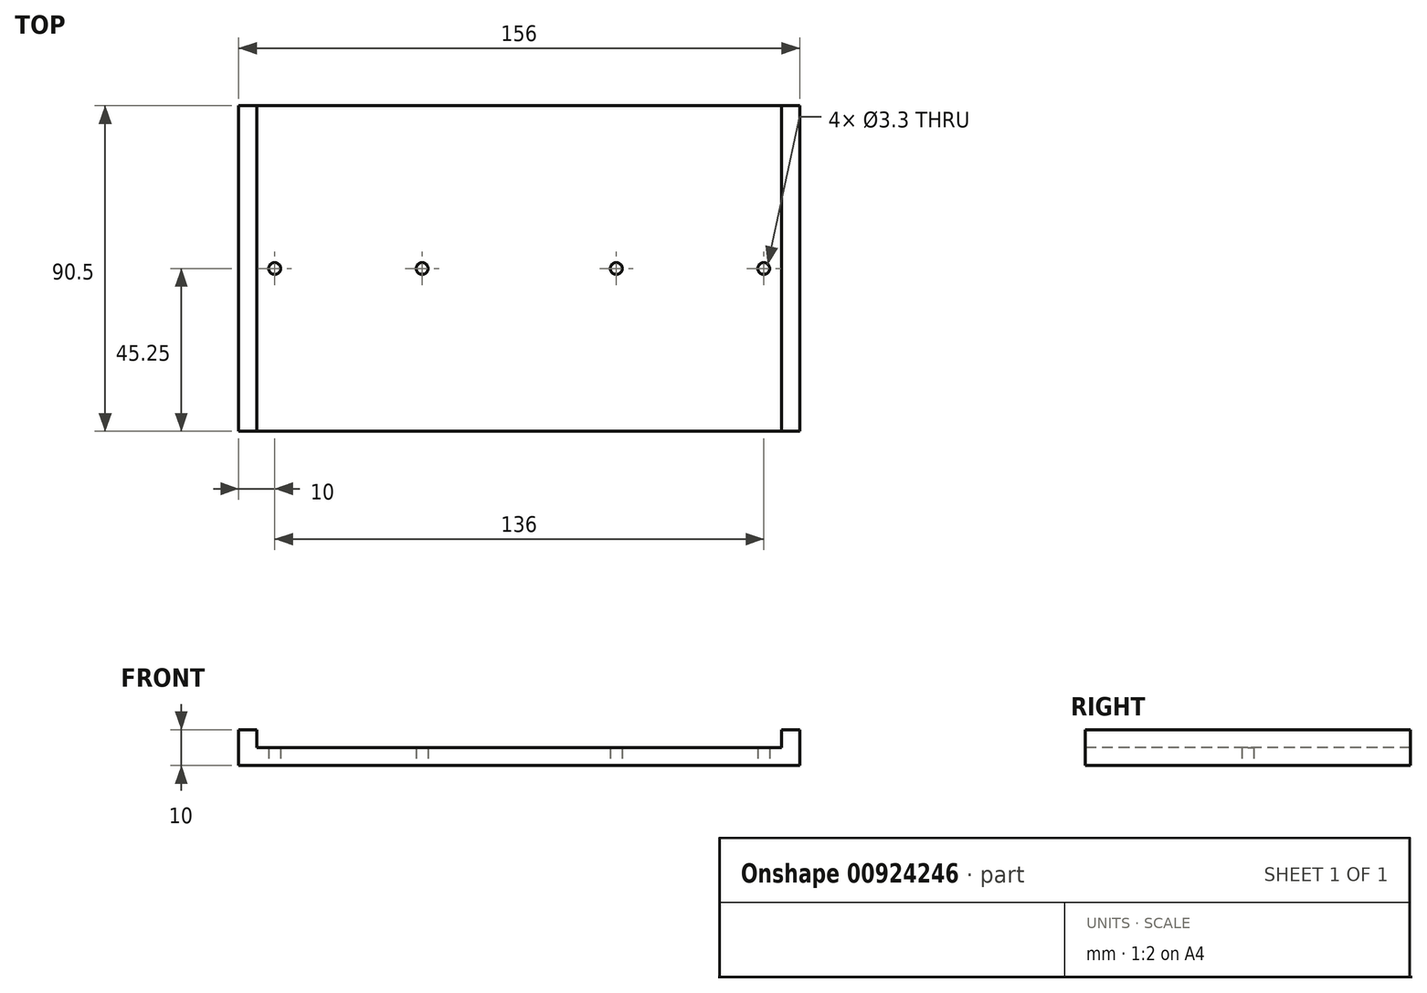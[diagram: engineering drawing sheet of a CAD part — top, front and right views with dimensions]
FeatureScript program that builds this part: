
annotation { "Feature Type Name" : "Feature", "Feature Type Description" : "" }
export const myFeature = defineFeature(function(context is Context, id is Id, definition is map)
    precondition{}
    {
        {
            var Q0;
            Q0=qCreatedBy(makeId("Top.planeOp"),FACE);
            var sketch = newSketch(context, id + "F0", { "sketchPlane" : qUnion([Q0])});
            skLineSegment(sketch, "E0.bottom", {"start": v(78, -45.25) * mm, "end": v(-78, -45.25) * mm});
            skLineSegment(sketch, "E0.top", {"start": v(78, 45.25) * mm, "end": v(-78, 45.25) * mm});
            skLineSegment(sketch, "E0.left", {"start": v(78, -45.25) * mm, "end": v(78, 45.25) * mm});
            skLineSegment(sketch, "E0.right", {"start": v(-78, -45.25) * mm, "end": v(-78, 45.25) * mm});
            skPoint(sketch, "E0.middle", {"position": v(0, 0) * mm});
            skLineSegment(sketch, "E1", {"start": v(-73, 45.25) * mm, "end": v(-73, -45.25) * mm});
            skLineSegment(sketch, "E2", {"start": v(73, 45.25) * mm, "end": v(73, -45.25) * mm});
            skSolve(sketch);
        }
        {
            var Q0;
            Q0 = qSketchRegion(id + "F0", true);
            extrude(context, id + "F1", {"entities" : qUnion([Q0]), "depth" : 5 * mm, "offsetDistance" : 25 * mm});
        }
        {
            var Q0;
            Q0=makeQuery(id+"F1.opExtrude","CAP_FACE",FACE,{"disambiguationData":[OSD([sQuery(id+"F0.wireOp",EDGE,"E0.bottom"),sQuery(id+"F0.wireOp",EDGE,"E0.top"),sQuery(id+"F0.wireOp",EDGE,"E0.left"),sQuery(id+"F0.wireOp",EDGE,"E0.right")])],"isStart":false});
            var sketch = newSketch(context, id + "F2", { "sketchPlane" : qUnion([Q0])});
            skLineSegment(sketch, "E3", {"start": v(-73, 45.25) * mm, "end": v(-73, -45.25) * mm});
            skLineSegment(sketch, "E4", {"start": v(73, 45.25) * mm, "end": v(73, -45.25) * mm});
            skSolve(sketch);
        }
        {
            var Q0;
            Q0 = qSketchRegion(id + "F2", true);
            var Q1;
            {var subQ0=sQuery(id+"F2.wireOp",EDGE,"E3");Q1=makeQuery(id+"F2.imprint","IMPRINT",FACE,{"disambiguationData":[TD([[makeQuery(id+"F2.imprint","IMPRINT",EDGE,{"derivedFrom":subQ0}),-1.0]])]});}
            var Q2;
            {var subQ0=sQuery(id+"F2.wireOp",EDGE,"E4");Q2=makeQuery(id+"F2.imprint","IMPRINT",FACE,{"disambiguationData":[TD([[makeQuery(id+"F2.imprint","IMPRINT",EDGE,{"derivedFrom":subQ0}),1.0]])]});}
            extrude(context, id + "F3", {"entities" : qUnion([Q0, Q1, Q2]), "operationType" : NewBodyOperationType.ADD, "depth" : 5 * mm, "offsetDistance" : 25 * mm});
        }
        {
            var Q0;
            Q0=makeQuery(id+"F1.opExtrude","CAP_FACE",FACE,{"disambiguationData":[OSD([sQuery(id+"F0.wireOp",EDGE,"E0.bottom"),sQuery(id+"F0.wireOp",EDGE,"E0.top"),sQuery(id+"F0.wireOp",EDGE,"E0.left"),sQuery(id+"F0.wireOp",EDGE,"E0.right")])],"isStart":true});
            var sketch = newSketch(context, id + "F4", { "sketchPlane" : qUnion([Q0])});
            skLineSegment(sketch, "E5", {"start": v(-78, 0) * mm, "end": v(78, 0) * mm, "construction": true});
            skPoint(sketch, "E6", {"position": v(-68, 0) * mm});
            skPoint(sketch, "E7", {"position": v(-27, 0) * mm});
            skPoint(sketch, "E8", {"position": v(27, 0) * mm});
            skPoint(sketch, "E9", {"position": v(68, 0) * mm});
            skCircle(sketch, "E10", {"center": v(-68, 0) * mm, "radius": 1.65 * mm});
            skCircle(sketch, "E11", {"center": v(-27, 0) * mm, "radius": 1.65 * mm});
            skCircle(sketch, "E12", {"center": v(27, 0) * mm, "radius": 1.65 * mm});
            skCircle(sketch, "E13", {"center": v(68, 0) * mm, "radius": 1.65 * mm});
            skSolve(sketch);
        }
        {
            var Q0;
            Q0 = qSketchRegion(id + "F4", true);
            extrude(context, id + "F5", {"entities" : qUnion([Q0]), "operationType" : NewBodyOperationType.REMOVE, "endBound" : BoundingType.THROUGH_ALL, "oppositeDirection" : true, "depth" : 25 * mm, "offsetDistance" : 25 * mm});
        }
    });
